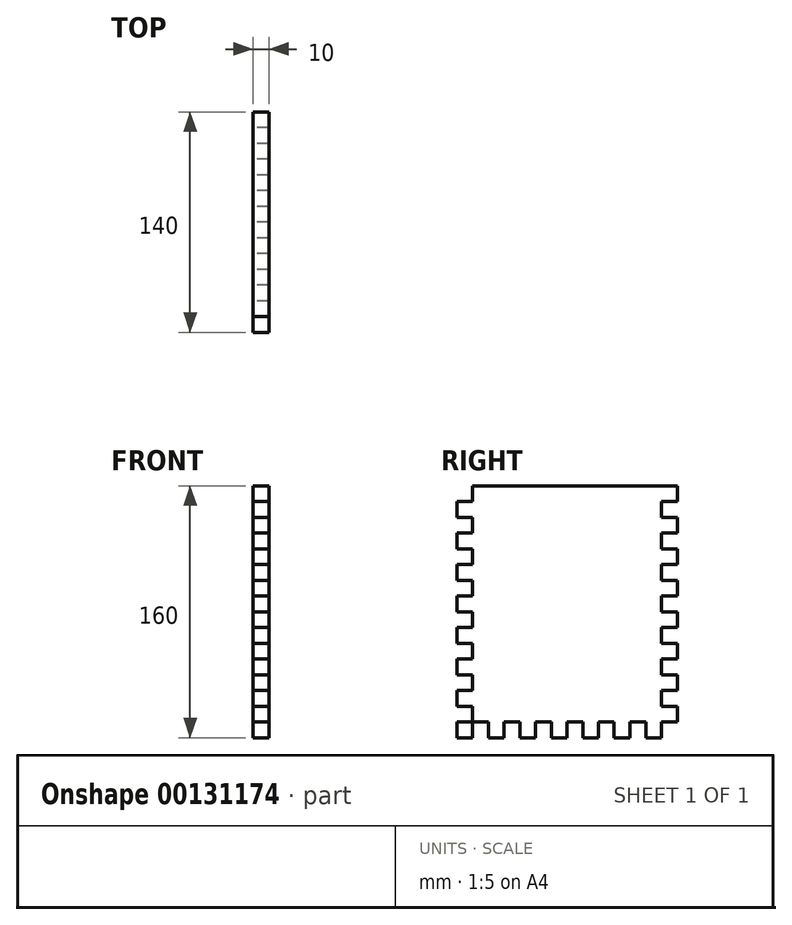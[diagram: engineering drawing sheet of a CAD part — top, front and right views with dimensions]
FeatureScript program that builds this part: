
annotation { "Feature Type Name" : "Feature", "Feature Type Description" : "" }
export const myFeature = defineFeature(function(context is Context, id is Id, definition is map)
    precondition{}
    {
        {
            var Q0;
            Q0=qCreatedBy(makeId("Right.planeOp"),FACE);
            var sketch = newSketch(context, id + "F0", { "sketchPlane" : qUnion([Q0])});
            skLineSegment(sketch, "E0.bottom", {"start": v(60, -80) * mm, "end": v(50, -80) * mm});
            skLineSegment(sketch, "E0.top", {"start": v(70, 80) * mm, "end": v(-60, 80) * mm});
            skLineSegment(sketch, "E0.left", {"start": v(70, -70) * mm, "end": v(70, -60) * mm});
            skLineSegment(sketch, "E0.right", {"start": v(-70, -80) * mm, "end": v(-70, -70) * mm});
            skPoint(sketch, "E0.middle", {"position": v(0, 0) * mm});
            skLineSegment(sketch, "E1.top", {"start": v(-70, 70) * mm, "end": v(-60, 70) * mm});
            skLineSegment(sketch, "E1.right", {"start": v(-60, 80) * mm, "end": v(-60, 70) * mm});
            skLineSegment(sketch, "E2.bottom", {"start": v(-60, 70) * mm, "end": v(-70, 70) * mm});
            skLineSegment(sketch, "E2.top", {"start": v(-60, 60) * mm, "end": v(-70, 60) * mm});
            skLineSegment(sketch, "E2.left", {"start": v(-60, 70) * mm, "end": v(-60, 60) * mm});
            skLineSegment(sketch, "E2.right", {"start": v(-70, 70) * mm, "end": v(-70, 60) * mm});
            skLineSegment(sketch, "E3.top", {"start": v(-60, 50) * mm, "end": v(-70, 50) * mm});
            skLineSegment(sketch, "E3.left", {"start": v(-60, 60) * mm, "end": v(-60, 50) * mm});
            skLineSegment(sketch, "E4.top", {"start": v(-60, 40) * mm, "end": v(-70, 40) * mm});
            skLineSegment(sketch, "E4.left", {"start": v(-60, 50) * mm, "end": v(-60, 40) * mm});
            skLineSegment(sketch, "E4.right", {"start": v(-70, 50) * mm, "end": v(-70, 40) * mm});
            skLineSegment(sketch, "E5.top", {"start": v(-60, 30) * mm, "end": v(-70, 30) * mm});
            skLineSegment(sketch, "E5.left", {"start": v(-60, 40) * mm, "end": v(-60, 30) * mm});
            skLineSegment(sketch, "E6.top", {"start": v(-60, 20) * mm, "end": v(-70, 20) * mm});
            skLineSegment(sketch, "E6.left", {"start": v(-60, 30) * mm, "end": v(-60, 20) * mm});
            skLineSegment(sketch, "E6.right", {"start": v(-70, 30) * mm, "end": v(-70, 20) * mm});
            skLineSegment(sketch, "E7.top", {"start": v(-60, 10) * mm, "end": v(-70, 10) * mm});
            skLineSegment(sketch, "E7.left", {"start": v(-60, 20) * mm, "end": v(-60, 10) * mm});
            skLineSegment(sketch, "E8.top", {"start": v(-60, 0) * mm, "end": v(-70, 0) * mm});
            skLineSegment(sketch, "E8.left", {"start": v(-60, 10) * mm, "end": v(-60, 0) * mm});
            skLineSegment(sketch, "E8.right", {"start": v(-70, 10) * mm, "end": v(-70, 0) * mm});
            skLineSegment(sketch, "E9.top", {"start": v(-60, -10) * mm, "end": v(-70, -10) * mm});
            skLineSegment(sketch, "E9.left", {"start": v(-60, 0) * mm, "end": v(-60, -10) * mm});
            skLineSegment(sketch, "E10.top", {"start": v(-60, -20) * mm, "end": v(-70, -20) * mm});
            skLineSegment(sketch, "E10.left", {"start": v(-60, -10) * mm, "end": v(-60, -20) * mm});
            skLineSegment(sketch, "E10.right", {"start": v(-70, -10) * mm, "end": v(-70, -20) * mm});
            skLineSegment(sketch, "E11.top", {"start": v(-60, -30) * mm, "end": v(-70, -30) * mm});
            skLineSegment(sketch, "E11.left", {"start": v(-60, -20) * mm, "end": v(-60, -30) * mm});
            skLineSegment(sketch, "E12.top", {"start": v(-60, -40) * mm, "end": v(-70, -40) * mm});
            skLineSegment(sketch, "E12.left", {"start": v(-60, -30) * mm, "end": v(-60, -40) * mm});
            skLineSegment(sketch, "E12.right", {"start": v(-70, -30) * mm, "end": v(-70, -40) * mm});
            skLineSegment(sketch, "E13.top", {"start": v(-60, -50) * mm, "end": v(-70, -50) * mm});
            skLineSegment(sketch, "E13.left", {"start": v(-60, -40) * mm, "end": v(-60, -50) * mm});
            skLineSegment(sketch, "E14.top", {"start": v(-60, -60) * mm, "end": v(-70, -60) * mm});
            skLineSegment(sketch, "E14.left", {"start": v(-60, -50) * mm, "end": v(-60, -60) * mm});
            skLineSegment(sketch, "E14.right", {"start": v(-70, -50) * mm, "end": v(-70, -60) * mm});
            skLineSegment(sketch, "E15.top", {"start": v(-60, -70) * mm, "end": v(-70, -70) * mm});
            skLineSegment(sketch, "E15.left", {"start": v(-60, -60) * mm, "end": v(-60, -70) * mm});
            skLineSegment(sketch, "E16.top", {"start": v(-60, -80) * mm, "end": v(-70, -80) * mm});
            skLineSegment(sketch, "E16.left", {"start": v(-60, -70) * mm, "end": v(-60, -80) * mm});
            skLineSegment(sketch, "E16.right", {"start": v(-70, -70) * mm, "end": v(-70, -80) * mm});
            skLineSegment(sketch, "E17.bottom", {"start": v(-60, 70) * mm, "end": v(-50, 70) * mm});
            skLineSegment(sketch, "E17.top", {"start": v(-60, 80) * mm, "end": v(-50, 80) * mm});
            skLineSegment(sketch, "E17.left", {"start": v(-60, 70) * mm, "end": v(-60, 80) * mm});
            skLineSegment(sketch, "E17.right", {"start": v(-50, 70) * mm, "end": v(-50, 80) * mm});
            skLineSegment(sketch, "E18.bottom", {"start": v(-50, 70) * mm, "end": v(-40, 70) * mm});
            skLineSegment(sketch, "E18.top", {"start": v(-50, 80) * mm, "end": v(-40, 80) * mm});
            skLineSegment(sketch, "E18.right", {"start": v(-40, 70) * mm, "end": v(-40, 80) * mm});
            skLineSegment(sketch, "E19.bottom", {"start": v(-40, 70) * mm, "end": v(-30, 70) * mm});
            skLineSegment(sketch, "E19.top", {"start": v(-40, 80) * mm, "end": v(-30, 80) * mm});
            skLineSegment(sketch, "E19.right", {"start": v(-30, 70) * mm, "end": v(-30, 80) * mm});
            skLineSegment(sketch, "E20.bottom", {"start": v(-30, 70) * mm, "end": v(-20, 70) * mm});
            skLineSegment(sketch, "E20.top", {"start": v(-30, 80) * mm, "end": v(-20, 80) * mm});
            skLineSegment(sketch, "E20.right", {"start": v(-20, 70) * mm, "end": v(-20, 80) * mm});
            skLineSegment(sketch, "E21.bottom", {"start": v(-20, 70) * mm, "end": v(-10, 70) * mm});
            skLineSegment(sketch, "E21.top", {"start": v(-20, 80) * mm, "end": v(-10, 80) * mm});
            skLineSegment(sketch, "E21.right", {"start": v(-10, 70) * mm, "end": v(-10, 80) * mm});
            skLineSegment(sketch, "E22.bottom", {"start": v(-10, 70) * mm, "end": v(0, 70) * mm});
            skLineSegment(sketch, "E22.top", {"start": v(-10, 80) * mm, "end": v(0, 80) * mm});
            skLineSegment(sketch, "E22.right", {"start": v(0, 70) * mm, "end": v(0, 80) * mm});
            skLineSegment(sketch, "E23.bottom", {"start": v(0, 70) * mm, "end": v(10, 70) * mm});
            skLineSegment(sketch, "E23.top", {"start": v(0, 80) * mm, "end": v(10, 80) * mm});
            skLineSegment(sketch, "E23.right", {"start": v(10, 70) * mm, "end": v(10, 80) * mm});
            skLineSegment(sketch, "E24.bottom", {"start": v(10, 70) * mm, "end": v(20, 70) * mm});
            skLineSegment(sketch, "E24.top", {"start": v(10, 80) * mm, "end": v(20, 80) * mm});
            skLineSegment(sketch, "E24.right", {"start": v(20, 70) * mm, "end": v(20, 80) * mm});
            skLineSegment(sketch, "E25.bottom", {"start": v(20, 70) * mm, "end": v(30, 70) * mm});
            skLineSegment(sketch, "E25.top", {"start": v(20, 80) * mm, "end": v(30, 80) * mm});
            skLineSegment(sketch, "E25.right", {"start": v(30, 70) * mm, "end": v(30, 80) * mm});
            skLineSegment(sketch, "E26.bottom", {"start": v(30, 70) * mm, "end": v(40, 70) * mm});
            skLineSegment(sketch, "E26.top", {"start": v(30, 80) * mm, "end": v(40, 80) * mm});
            skLineSegment(sketch, "E26.right", {"start": v(40, 70) * mm, "end": v(40, 80) * mm});
            skLineSegment(sketch, "E27.bottom", {"start": v(40, 70) * mm, "end": v(50, 70) * mm});
            skLineSegment(sketch, "E27.top", {"start": v(40, 80) * mm, "end": v(50, 80) * mm});
            skLineSegment(sketch, "E27.right", {"start": v(50, 70) * mm, "end": v(50, 80) * mm});
            skLineSegment(sketch, "E28.bottom", {"start": v(50, 70) * mm, "end": v(60, 70) * mm});
            skLineSegment(sketch, "E28.top", {"start": v(50, 80) * mm, "end": v(60, 80) * mm});
            skLineSegment(sketch, "E28.right", {"start": v(60, 70) * mm, "end": v(60, 80) * mm});
            skLineSegment(sketch, "E29.bottom", {"start": v(60, 70) * mm, "end": v(70, 70) * mm});
            skLineSegment(sketch, "E29.top", {"start": v(60, 80) * mm, "end": v(70, 80) * mm});
            skLineSegment(sketch, "E29.right", {"start": v(70, 70) * mm, "end": v(70, 80) * mm});
            skLineSegment(sketch, "E30.top", {"start": v(60, 60) * mm, "end": v(70, 60) * mm});
            skLineSegment(sketch, "E30.left", {"start": v(60, 70) * mm, "end": v(60, 60) * mm});
            skLineSegment(sketch, "E31.top", {"start": v(60, 50) * mm, "end": v(70, 50) * mm});
            skLineSegment(sketch, "E31.left", {"start": v(60, 60) * mm, "end": v(60, 50) * mm});
            skLineSegment(sketch, "E31.right", {"start": v(70, 60) * mm, "end": v(70, 50) * mm});
            skLineSegment(sketch, "E32.top", {"start": v(60, 40) * mm, "end": v(70, 40) * mm});
            skLineSegment(sketch, "E32.left", {"start": v(60, 50) * mm, "end": v(60, 40) * mm});
            skLineSegment(sketch, "E33.top", {"start": v(60, 30) * mm, "end": v(70, 30) * mm});
            skLineSegment(sketch, "E33.left", {"start": v(60, 40) * mm, "end": v(60, 30) * mm});
            skLineSegment(sketch, "E33.right", {"start": v(70, 40) * mm, "end": v(70, 30) * mm});
            skLineSegment(sketch, "E34.top", {"start": v(60, 20) * mm, "end": v(70, 20) * mm});
            skLineSegment(sketch, "E34.left", {"start": v(60, 30) * mm, "end": v(60, 20) * mm});
            skLineSegment(sketch, "E35.top", {"start": v(60, 10) * mm, "end": v(70, 10) * mm});
            skLineSegment(sketch, "E35.left", {"start": v(60, 20) * mm, "end": v(60, 10) * mm});
            skLineSegment(sketch, "E35.right", {"start": v(70, 20) * mm, "end": v(70, 10) * mm});
            skLineSegment(sketch, "E36.top", {"start": v(60, 0) * mm, "end": v(70, 0) * mm});
            skLineSegment(sketch, "E36.left", {"start": v(60, 10) * mm, "end": v(60, 0) * mm});
            skLineSegment(sketch, "E37.top", {"start": v(60, -10) * mm, "end": v(70, -10) * mm});
            skLineSegment(sketch, "E37.left", {"start": v(60, 0) * mm, "end": v(60, -10) * mm});
            skLineSegment(sketch, "E37.right", {"start": v(70, 0) * mm, "end": v(70, -10) * mm});
            skLineSegment(sketch, "E38.top", {"start": v(60, -20) * mm, "end": v(70, -20) * mm});
            skLineSegment(sketch, "E38.left", {"start": v(60, -10) * mm, "end": v(60, -20) * mm});
            skLineSegment(sketch, "E39.top", {"start": v(60, -30) * mm, "end": v(70, -30) * mm});
            skLineSegment(sketch, "E39.left", {"start": v(60, -20) * mm, "end": v(60, -30) * mm});
            skLineSegment(sketch, "E39.right", {"start": v(70, -20) * mm, "end": v(70, -30) * mm});
            skLineSegment(sketch, "E40.top", {"start": v(60, -40) * mm, "end": v(70, -40) * mm});
            skLineSegment(sketch, "E40.left", {"start": v(60, -30) * mm, "end": v(60, -40) * mm});
            skLineSegment(sketch, "E41.top", {"start": v(60, -50) * mm, "end": v(70, -50) * mm});
            skLineSegment(sketch, "E41.left", {"start": v(60, -40) * mm, "end": v(60, -50) * mm});
            skLineSegment(sketch, "E41.right", {"start": v(70, -40) * mm, "end": v(70, -50) * mm});
            skLineSegment(sketch, "E42.top", {"start": v(60, -60) * mm, "end": v(70, -60) * mm});
            skLineSegment(sketch, "E42.left", {"start": v(60, -50) * mm, "end": v(60, -60) * mm});
            skLineSegment(sketch, "E43.top", {"start": v(60, -70) * mm, "end": v(70, -70) * mm});
            skLineSegment(sketch, "E43.left", {"start": v(60, -60) * mm, "end": v(60, -70) * mm});
            skLineSegment(sketch, "E43.right", {"start": v(70, -60) * mm, "end": v(70, -70) * mm});
            skLineSegment(sketch, "E44.bottom", {"start": v(60, -70) * mm, "end": v(60, -70) * mm});
            skLineSegment(sketch, "E44.top", {"start": v(60, -80) * mm, "end": v(60, -80) * mm});
            skLineSegment(sketch, "E44.left", {"start": v(60, -70) * mm, "end": v(60, -80) * mm});
            skLineSegment(sketch, "E44.right", {"start": v(60, -70) * mm, "end": v(60, -80) * mm});
            skLineSegment(sketch, "E45.bottom", {"start": v(-60, -70) * mm, "end": v(-50, -70) * mm});
            skLineSegment(sketch, "E45.right", {"start": v(-50, -70) * mm, "end": v(-50, -80) * mm});
            skLineSegment(sketch, "E46.bottom", {"start": v(-50, -70) * mm, "end": v(-40, -70) * mm});
            skLineSegment(sketch, "E46.top", {"start": v(-50, -80) * mm, "end": v(-40, -80) * mm});
            skLineSegment(sketch, "E46.right", {"start": v(-40, -70) * mm, "end": v(-40, -80) * mm});
            skLineSegment(sketch, "E47.bottom", {"start": v(-40, -70) * mm, "end": v(-30, -70) * mm});
            skLineSegment(sketch, "E47.right", {"start": v(-30, -70) * mm, "end": v(-30, -80) * mm});
            skLineSegment(sketch, "E48.bottom", {"start": v(-30, -70) * mm, "end": v(-20, -70) * mm});
            skLineSegment(sketch, "E48.top", {"start": v(-30, -80) * mm, "end": v(-20, -80) * mm});
            skLineSegment(sketch, "E48.right", {"start": v(-20, -70) * mm, "end": v(-20, -80) * mm});
            skLineSegment(sketch, "E49.bottom", {"start": v(-20, -70) * mm, "end": v(-10, -70) * mm});
            skLineSegment(sketch, "E49.right", {"start": v(-10, -70) * mm, "end": v(-10, -80) * mm});
            skLineSegment(sketch, "E50.bottom", {"start": v(-10, -70) * mm, "end": v(0, -70) * mm});
            skLineSegment(sketch, "E50.top", {"start": v(-10, -80) * mm, "end": v(0, -80) * mm});
            skLineSegment(sketch, "E50.right", {"start": v(0, -70) * mm, "end": v(0, -80) * mm});
            skLineSegment(sketch, "E51.bottom", {"start": v(0, -70) * mm, "end": v(10, -70) * mm});
            skLineSegment(sketch, "E51.right", {"start": v(10, -70) * mm, "end": v(10, -80) * mm});
            skLineSegment(sketch, "E52.bottom", {"start": v(10, -70) * mm, "end": v(20, -70) * mm});
            skLineSegment(sketch, "E52.top", {"start": v(10, -80) * mm, "end": v(20, -80) * mm});
            skLineSegment(sketch, "E52.right", {"start": v(20, -70) * mm, "end": v(20, -80) * mm});
            skLineSegment(sketch, "E53.bottom", {"start": v(20, -70) * mm, "end": v(30, -70) * mm});
            skLineSegment(sketch, "E53.right", {"start": v(30, -70) * mm, "end": v(30, -80) * mm});
            skLineSegment(sketch, "E54.bottom", {"start": v(30, -70) * mm, "end": v(40, -70) * mm});
            skLineSegment(sketch, "E54.top", {"start": v(30, -80) * mm, "end": v(40, -80) * mm});
            skLineSegment(sketch, "E54.right", {"start": v(40, -70) * mm, "end": v(40, -80) * mm});
            skLineSegment(sketch, "E55.bottom", {"start": v(40, -70) * mm, "end": v(50, -70) * mm});
            skLineSegment(sketch, "E55.right", {"start": v(50, -70) * mm, "end": v(50, -80) * mm});
            skLineSegment(sketch, "E56.bottom", {"start": v(50, -70) * mm, "end": v(60, -70) * mm});
            skLineSegment(sketch, "E56.top", {"start": v(50, -70) * mm, "end": v(60, -70) * mm});
            skLineSegment(sketch, "E56.left", {"start": v(50, -70) * mm, "end": v(50, -70) * mm});
            skLineSegment(sketch, "E57.trimOffspring", {"start": v(-40, -80) * mm, "end": v(-50, -80) * mm});
            skLineSegment(sketch, "E58.trimOffspring", {"start": v(-20, -80) * mm, "end": v(-30, -80) * mm});
            skLineSegment(sketch, "E59.trimOffspring", {"start": v(0, -80) * mm, "end": v(-10, -80) * mm});
            skLineSegment(sketch, "E60.trimOffspring", {"start": v(20, -80) * mm, "end": v(10, -80) * mm});
            skPoint(sketch, "E61.orphan", {"position": v(70, -80) * mm});
            skLineSegment(sketch, "E62.trimOffspring", {"start": v(-70, -60) * mm, "end": v(-70, -50) * mm});
            skLineSegment(sketch, "E63.trimOffspring", {"start": v(-70, -40) * mm, "end": v(-70, -30) * mm});
            skLineSegment(sketch, "E64.trimOffspring", {"start": v(-70, -20) * mm, "end": v(-70, -10) * mm});
            skLineSegment(sketch, "E65.trimOffspring", {"start": v(-70, 0) * mm, "end": v(-70, 10) * mm});
            skLineSegment(sketch, "E66.trimOffspring", {"start": v(-70, 20) * mm, "end": v(-70, 30) * mm});
            skLineSegment(sketch, "E67.trimOffspring", {"start": v(-70, 40) * mm, "end": v(-70, 50) * mm});
            skLineSegment(sketch, "E68.trimOffspring", {"start": v(-70, 60) * mm, "end": v(-70, 70) * mm});
            skPoint(sketch, "E69.orphan", {"position": v(-70, 80) * mm});
            skLineSegment(sketch, "E70.trimOffspring", {"start": v(70, -50) * mm, "end": v(70, -40) * mm});
            skLineSegment(sketch, "E71.trimOffspring", {"start": v(70, -30) * mm, "end": v(70, -20) * mm});
            skLineSegment(sketch, "E72.trimOffspring", {"start": v(70, -10) * mm, "end": v(70, 0) * mm});
            skLineSegment(sketch, "E73.trimOffspring", {"start": v(70, 10) * mm, "end": v(70, 20) * mm});
            skLineSegment(sketch, "E74.trimOffspring", {"start": v(70, 30) * mm, "end": v(70, 40) * mm});
            skLineSegment(sketch, "E75.trimOffspring", {"start": v(70, 50) * mm, "end": v(70, 60) * mm});
            skSolve(sketch);
        }
        {
            var Q0;
            Q0 = qSketchRegion(id + "F0", true);
            extrude(context, id + "F1", {"entities" : qUnion([Q0]), "depth" : 10 * mm});
        }
    });
